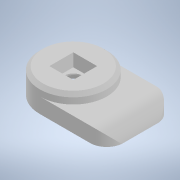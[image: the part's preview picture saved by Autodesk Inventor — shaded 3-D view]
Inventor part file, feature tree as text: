
AUTODESK INVENTOR PART (.ipt)
format: ipt  version: 2021 (Build 250183000, 183)  size: 151,552 bytes
history: native  units: mm
features: other x7, sketch x5, extrude x3, revolve x1, hole x1
ambient origin geometry x8: Origin, YZ Plane, XZ Plane, XY Plane, X Axis, Y Axis, Z Axis, Center Point
bodies: Solid1 (feature_tree)
feature tree (17):
  revolve  "Revolution1"  [1 undecoded]
  extrude  "Extrusion1"  Depth=6.5mm TaperAngle=0.0deg
  hole  "Hole1"  [1 undecoded]
  extrude  "Extrusion2"  [1 undecoded]
  extrude  "Extrusion3"  [1 undecoded]
  other  "bottom_to_ins_XY"
  other  "bottom_to_ins_YZ"
  other  "bottom_to_ins_ZX"
  other  "bottom_to_ins_X"
  other  "bottom_to_ins_Y"
  other  "bottom_to_ins_Z"
  other  "bottom_to_ins_Center"
  sketch  "Sketch_1"  dims[d0=360.0deg d1=4.5mm d2=0.0mm]
  sketch  "Sketch_2"  dims[d3=5.5mm d4=6.0mm d5=11.7mm d6=2.0mm d7=90.0deg d8=3.5mm d9=0.0mm d10=6.5mm d11=0.0mm]
  sketch  "Sketch3"  dims[d12=20.0mm d13=0.0mm]
  sketch  "Sketch_9"
  sketch  "Sketch_3"
note: 4 required parameter values undecoded (feature->parameter linkage not recoverable at this tier; creation-order binding heuristic only, values carry confidence <= 0.55)